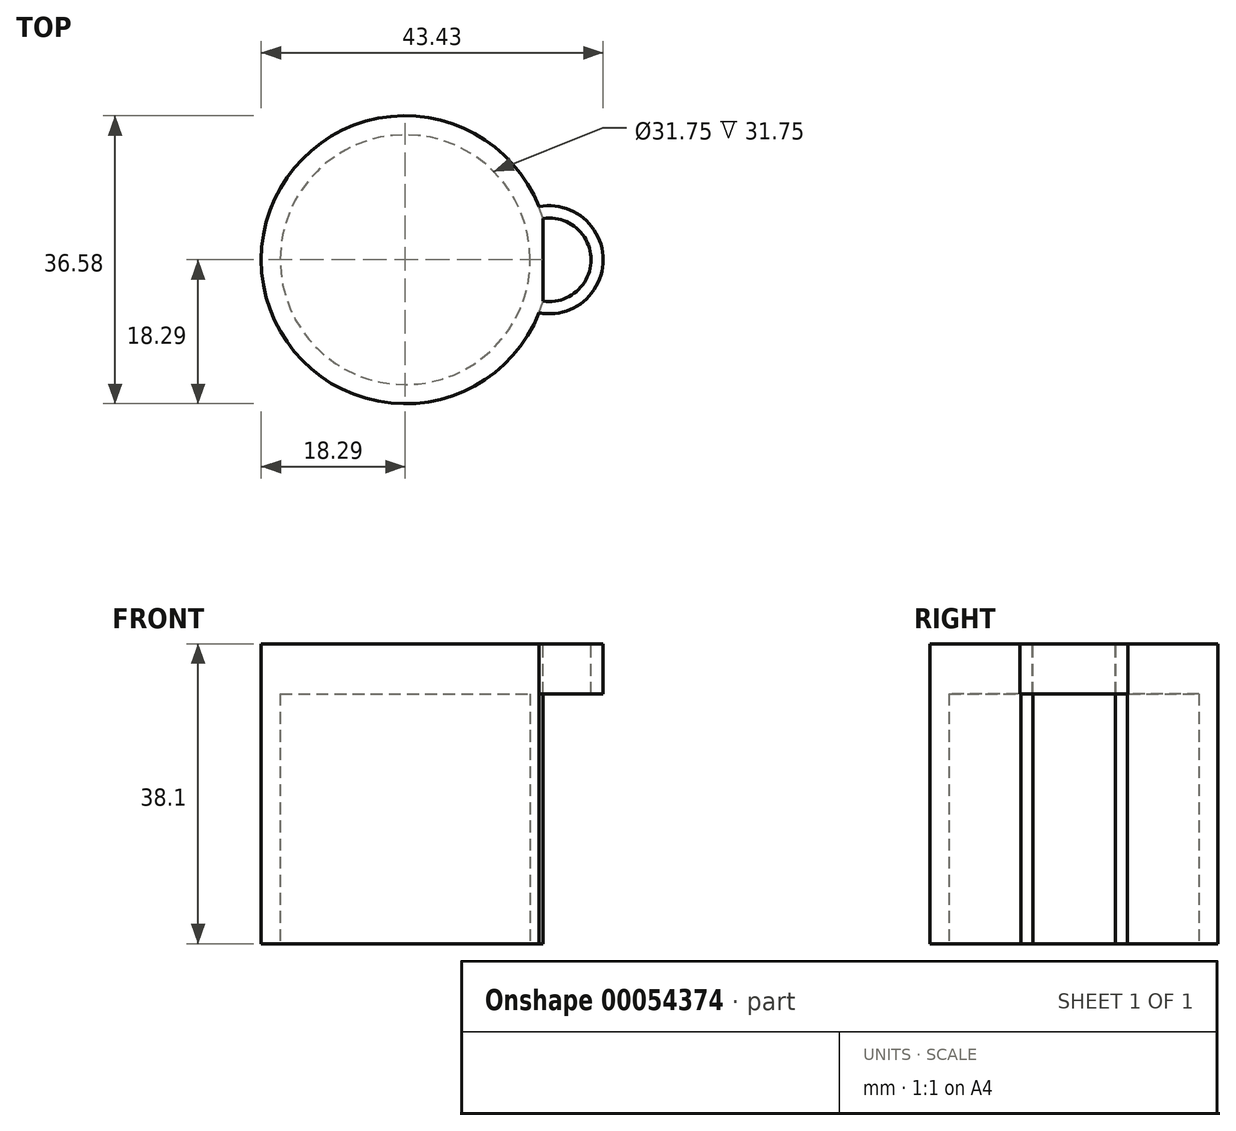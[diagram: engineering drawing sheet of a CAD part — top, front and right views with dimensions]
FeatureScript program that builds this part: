
annotation { "Feature Type Name" : "Feature", "Feature Type Description" : "" }
export const myFeature = defineFeature(function(context is Context, id is Id, definition is map)
    precondition{}
    {
        {
            var Q0;
            Q0=qCreatedBy(makeId("Top.planeOp"),FACE);
            var sketch = newSketch(context, id + "F0", { "sketchPlane" : qUnion([Q0])});
            skArc(sketch, "E0", {"start": v(17.52, 5.25) * mm, "mid": v(-18.29, 0) * mm, "end": v(17.52, -5.25) * mm});
            skArc(sketch, "E1", {"start": v(17, -6.73) * mm, "mid": v(25.14, 0) * mm, "end": v(17, 6.73) * mm});
            skArc(sketch, "E2", {"start": v(17.52, -5.25) * mm, "mid": v(23.6, 0) * mm, "end": v(17.52, 5.25) * mm});
            skLineSegment(sketch, "E3", {"start": v(17.52, -5.25) * mm, "end": v(17.52, 5.25) * mm});
            skSolve(sketch);
        }
        {
            var Q0;
            Q0 = qSketchRegion(id + "F0", true);
            extrude(context, id + "F1", {"entities" : qUnion([Q0]), "oppositeDirection" : true, "depth" : 38.1 * mm});
        }
        {
            var Q0;
            Q0=makeQuery(id+"F1.opExtrude","CAP_FACE",FACE,{"disambiguationData":[OSD([sQuery(id+"F0.wireOp",EDGE,"E0")])],"isStart":false});
            var sketch = newSketch(context, id + "F2", { "sketchPlane" : qUnion([Q0])});
            skCircle(sketch, "E4", {"center": v(0, 0) * mm, "radius": 15.88 * mm});
            skSolve(sketch);
        }
        {
            var Q0;
            Q0 = qSketchRegion(id + "F2", true);
            extrude(context, id + "F3", {"entities" : qUnion([Q0]), "operationType" : NewBodyOperationType.REMOVE, "oppositeDirection" : true, "depth" : 31.75 * mm});
        }
        {
            var Q0;
            Q0=makeQuery(id+"F1.opExtrude","CAP_FACE",FACE,{"disambiguationData":[OSD([sQuery(id+"F0.wireOp",EDGE,"E0"),sQuery(id+"F0.wireOp",EDGE,"E1"),sQuery(id+"F0.wireOp",EDGE,"E2"),sQuery(id+"F0.wireOp",EDGE,"E3")])],"isStart":false});
            var sketch = newSketch(context, id + "F4", { "sketchPlane" : qUnion([Q0])});
            skLineSegment(sketch, "E5", {"start": v(17, 6.73) * mm, "end": v(17.52, 5.25) * mm});
            skLineSegment(sketch, "E6", {"start": v(17.52, -5.25) * mm, "end": v(17, -6.73) * mm});
            skSolve(sketch);
        }
        {
            var Q0;
            Q0=makeQuery(id+"F4.imprint","IMPRINT",FACE,{"disambiguationData":[TD([[makeQuery(id+"F4.imprint","IMPRINT",EDGE,{"derivedFrom":sQuery(id+"F4.wireOp",EDGE,"E5")}),1.0]])]});
            extrude(context, id + "F5", {"entities" : qUnion([Q0]), "operationType" : NewBodyOperationType.REMOVE, "oppositeDirection" : true, "depth" : 31.75 * mm});
        }
    });
